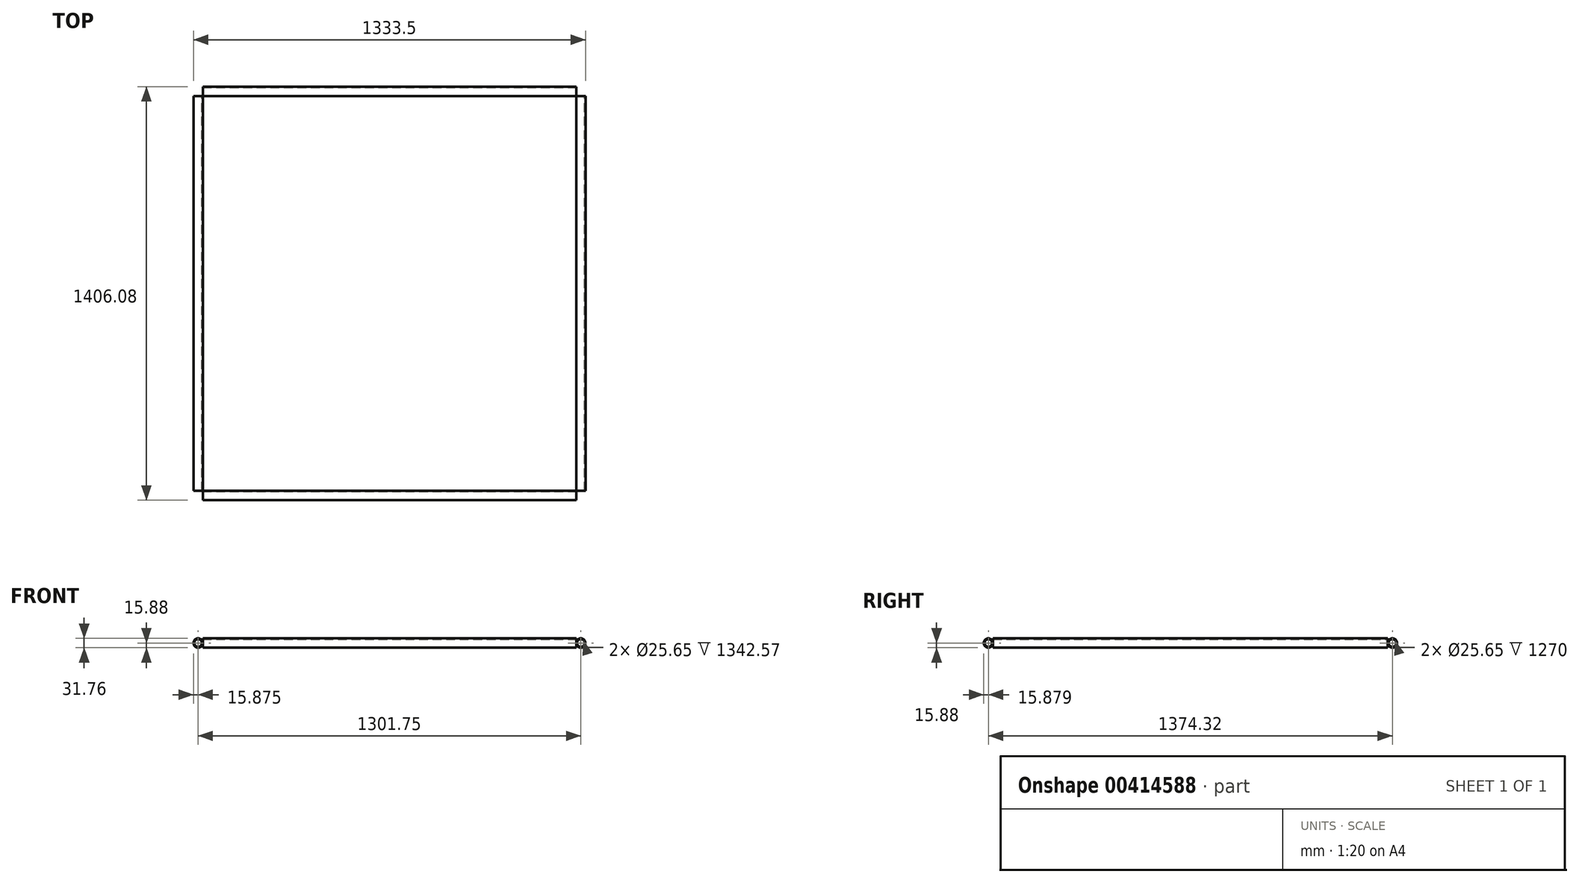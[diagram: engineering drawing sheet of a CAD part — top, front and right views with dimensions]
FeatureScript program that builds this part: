
annotation { "Feature Type Name" : "Feature", "Feature Type Description" : "" }
export const myFeature = defineFeature(function(context is Context, id is Id, definition is map)
    precondition{}
    {
        {
            var Q0;
            Q0=qCreatedBy(makeId("Top.planeOp"),FACE);
            var sketch = newSketch(context, id + "F0", { "sketchPlane" : qUnion([Q0])});
            skLineSegment(sketch, "E0.bottom", {"start": v(-635, 671.29) * mm, "end": v(635, 671.29) * mm});
            skLineSegment(sketch, "E0.top", {"start": v(-635, -671.29) * mm, "end": v(635, -671.29) * mm});
            skLineSegment(sketch, "E0.left", {"start": v(-635, 671.29) * mm, "end": v(-635, -671.29) * mm});
            skLineSegment(sketch, "E0.right", {"start": v(635, 671.29) * mm, "end": v(635, -671.29) * mm});
            skPoint(sketch, "E0.middle", {"position": v(0, 0) * mm});
            skSolve(sketch);
        }
        {
            var Q0;
            Q0=sQuery(id+"F0.wireOp",VERTEX,"E0.left.end");
            var Q1;
            Q1=qCreatedBy(makeId("Front.planeOp"),FACE);
            cPlane(context, id + "F1", {"entities" : qUnion([Q0, Q1]), "cplaneType" : CPlaneType.PLANE_POINT, "offset" : 25.4 * mm, "width" : 152.4 * mm, "height" : 152.4 * mm});
        }
        {
            var Q0;
            Q0=qCreatedBy(id+"F1.planeOp",FACE);
            var sketch = newSketch(context, id + "F2", { "sketchPlane" : qUnion([Q0])});
            skCircle(sketch, "E1", {"center": v(-650.88, 0) * mm, "radius": 15.88 * mm});
            skCircle(sketch, "E2", {"center": v(-650.88, 0) * mm, "radius": 12.83 * mm});
            skPoint(sketch, "E3", {"position": v(-635, 0) * mm});
            skSolve(sketch);
        }
        {
            var Q0;
            Q0=makeQuery(id+"F2.imprint","IMPRINT",FACE,{"disambiguationData":[TD([[makeQuery(id+"F2.imprint","IMPRINT",EDGE,{"derivedFrom":sQuery(id+"F2.wireOp",EDGE,"E1")}),1.0]])]});
            var Q1;
            Q1=sQuery(id+"F0.wireOp",EDGE,"E0.left");
            sweep(context, id + "F3", {"profiles" : qUnion([Q0]), "path" : qUnion([Q1])});
        }
        {
            var Q0;
            Q0=makeQuery(id+"F3.opSweep","SWEPT_BODY",BODY,{"disambiguationData":[OSD([sQuery(id+"F0.wireOp",EDGE,"E0.left"),sQuery(id+"F2.wireOp",EDGE,"E1"),sQuery(id+"F2.wireOp",EDGE,"E2")])]});
            var Q1;
            Q1=qCreatedBy(makeId("Right.planeOp"),FACE);
            mirror(context, id + "F4", {"entities" : qUnion([Q0]), "mirrorPlane" : qUnion([Q1])});
        }
        {
            var Q0;
            Q0=qCreatedBy(makeId("Right.planeOp"),FACE);
            var Q1;
            Q1=sQuery(id+"F0.wireOp",VERTEX,"E0.left.end");
            cPlane(context, id + "F5", {"entities" : qUnion([Q0, Q1]), "cplaneType" : CPlaneType.PLANE_POINT, "offset" : 25.4 * mm, "width" : 152.4 * mm, "height" : 152.4 * mm});
        }
        {
            var Q0;
            Q0=qCreatedBy(id+"F5.planeOp",FACE);
            var sketch = newSketch(context, id + "F6", { "sketchPlane" : qUnion([Q0])});
            skCircle(sketch, "E4", {"center": v(-687.16, 0) * mm, "radius": 15.88 * mm});
            skCircle(sketch, "E5", {"center": v(-687.16, 0) * mm, "radius": 12.83 * mm});
            skPoint(sketch, "E6", {"position": v(-671.29, 0) * mm});
            skSolve(sketch);
        }
        {
            var Q0;
            Q0=makeQuery(id+"F6.imprint","IMPRINT",FACE,{"disambiguationData":[TD([[makeQuery(id+"F6.imprint","IMPRINT",EDGE,{"derivedFrom":sQuery(id+"F6.wireOp",EDGE,"E4")}),1.0]])]});
            var Q1;
            Q1=sQuery(id+"F0.wireOp",EDGE,"E0.top");
            sweep(context, id + "F7", {"profiles" : qUnion([Q0]), "path" : qUnion([Q1])});
        }
        {
            var Q0;
            Q0=makeQuery(id+"F7.opSweep","SWEPT_BODY",BODY,{"disambiguationData":[OSD([sQuery(id+"F0.wireOp",EDGE,"E0.top"),sQuery(id+"F6.wireOp",EDGE,"E4"),sQuery(id+"F6.wireOp",EDGE,"E5")])]});
            var Q1;
            Q1=qCreatedBy(makeId("Front.planeOp"),FACE);
            mirror(context, id + "F8", {"entities" : qUnion([Q0]), "mirrorPlane" : qUnion([Q1])});
        }
    });
